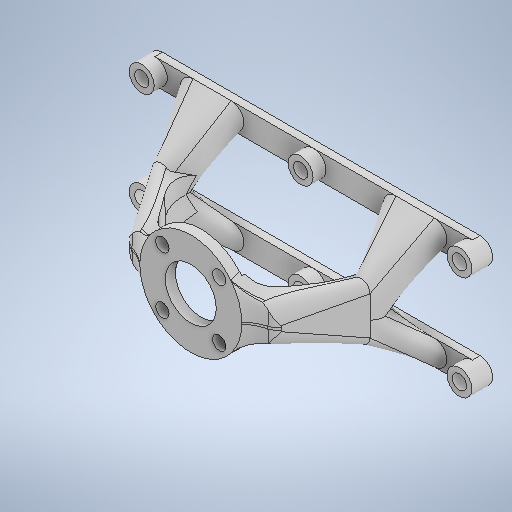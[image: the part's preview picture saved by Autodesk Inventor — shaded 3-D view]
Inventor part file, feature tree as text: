
AUTODESK INVENTOR PART (.ipt)
format: ipt  version: 2025.1 (Build 291241000, 241)  size: 1,218,048 bytes
history: native  units: mm
features: sketch x8, extrude x6, loft x6, fillet x5, plane x2
ambient origin geometry x8: Origin, YZ Plane, XZ Plane, XY Plane, X Axis, Y Axis, Z Axis, Center Point
bodies: Solid1 (feature_tree)
feature tree (27):
  sketch  "Sketch1"  dims[d0=20.0mm d1=40.0mm]
  extrude  "Extrusion1"  Depth=40.0mm
  extrude  "Extrusion2"  Depth=5.2mm
  plane  "Work Plane1"
  sketch  "Sketch2"  dims[d9=5.3mm d10=4.0mm d11=0.0mm]
  plane  "Work Plane2"
  sketch  "Sketch3"  dims[d12=8.0mm d13=0.0mm d14=47.2mm]
  extrude  "Extrusion3"  Depth=40.0mm TaperAngle=360.0deg
  sketch  "Sketch4"  dims[d15=9.8mm d17=5.6mm]
  loft  "Loft1"
  loft  "Loft2"
  loft  "Loft3"
  loft  "Loft4"
  loft  "Loft5"
  loft  "Loft6"
  fillet  "Fillet1"  Radius=3.0mm
  fillet  "Fillet2"  Radius=15.0mm
  fillet  "Fillet3"  Radius=15.0mm
  fillet  "Fillet4"  [1 undecoded]
  fillet  "Fillet5"  [1 undecoded]
  extrude  "Extrusion4"  TaperAngle=0.0deg  [1 undecoded]
  extrude  "Extrusion5"  TaperAngle=0.0deg  [1 undecoded]
  extrude  "Extrusion6"  TaperAngle=0.0deg  [1 undecoded]
  sketch  "Sketch Circular Pattern1"  dims[d2=31.5mm d3=5.2mm]
  sketch  "Sketch Rectangular Pattern1"  dims[d4=45.0deg d5=40.0mm d7=360.0deg]
  sketch  "Sketch5"  dims[d18=134.5mm d19=30.0mm d21=62.35mm d22=10.0mm d24=10.0mm]
  sketch  "Sketch6"  dims[d26=40.8mm d27=7.0mm d28=15.0mm d29=3.0mm d30=0.0mm d31=15.0mm d32=15.0mm d33=0.0mm d34=90.0deg d35=0.0mm d36=90.0deg d37=0.0mm d38=90.0deg d39=0.0mm d40=90.0deg d41=0.0mm d42=90.0deg d43=0.0mm d44=90.0deg d45=0.0mm d46=90.0deg d47=0.0mm d48=90.0deg d49=10.0mm d50=15.0mm d51=7.0mm d52=0.0mm d53=90.0deg d54=0.0mm d55=90.0deg d56=15.0mm d57=10.0mm d58=7.0mm d59=0.0mm d60=90.0deg d61=0.0mm d62=90.0deg d63=17.0mm d64=17.0mm d65=17.0mm d66=17.0mm d67=5.0mm d68=8.1mm d69=0.0mm d70=10.0mm d71=10.0mm d72=10.0mm d73=10.0mm d74=2.0mm d75=0.0mm d76=10.0mm d77=0.0mm]
note: 5 required parameter values undecoded (feature->parameter linkage not recoverable at this tier; creation-order binding heuristic only, values carry confidence <= 0.55)
